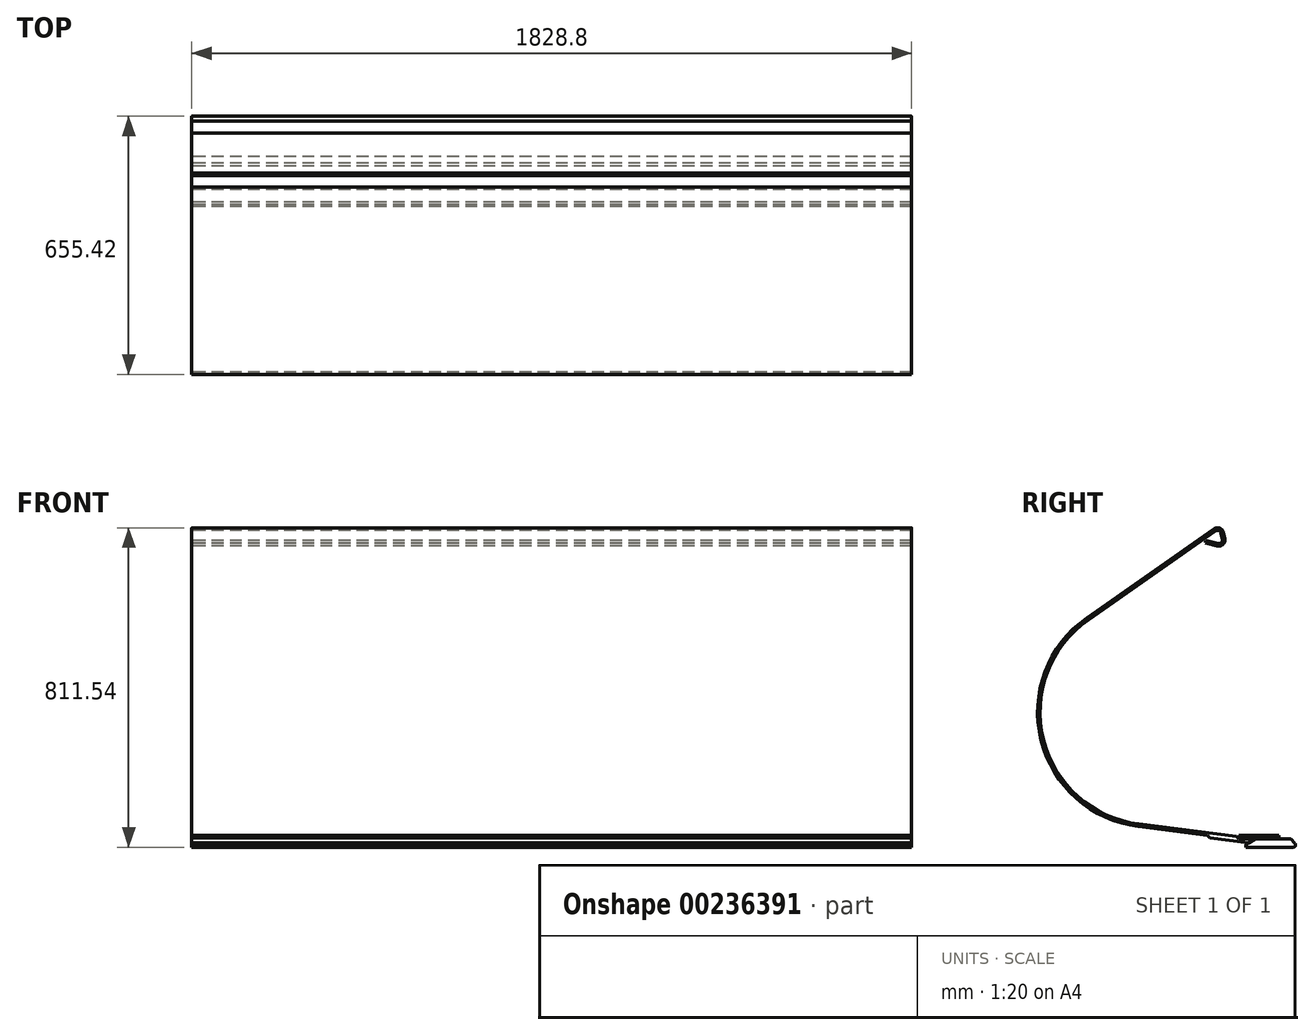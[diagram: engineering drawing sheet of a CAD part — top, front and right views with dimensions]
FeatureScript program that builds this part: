
annotation { "Feature Type Name" : "Feature", "Feature Type Description" : "" }
export const myFeature = defineFeature(function(context is Context, id is Id, definition is map)
    precondition{}
    {
        {
            var Q0;
            Q0=qCreatedBy(makeId("Right.planeOp"),FACE);
            var sketch = newSketch(context, id + "F0", { "sketchPlane" : qUnion([Q0])});
            skLineSegment(sketch, "E0", {"start": v(-127, 0) * mm, "end": v(-6, 0) * mm});
            skArc(sketch, "E1", {"start": v(-6, 0) * mm, "mid": v(-0.46, 3.7) * mm, "end": v(-1.76, 10.24) * mm});
            skLineSegment(sketch, "E2", {"start": v(-1.76, 10.24) * mm, "end": v(-12.51, 21) * mm});
            skLineSegment(sketch, "E3", {"start": v(-12.51, 21) * mm, "end": v(-102, 21) * mm});
            skLineSegment(sketch, "E4", {"start": v(-102, 21) * mm, "end": v(-127, 6.57) * mm});
            skLineSegment(sketch, "E5", {"start": v(-127, 6.57) * mm, "end": v(-127, 0) * mm});
            skSolve(sketch);
        }
        {
            var Q0;
            Q0 = qSketchRegion(id + "F0", true);
            extrude(context, id + "F1", {"entities" : qUnion([Q0]), "endBound" : BoundingType.SYMMETRIC, "depth" : 1828.8 * mm});
        }
        {
            var Q0;
            Q0=qCreatedBy(makeId("Right.planeOp"),FACE);
            var sketch = newSketch(context, id + "F2", { "sketchPlane" : qUnion([Q0])});
            skLineSegment(sketch, "E6.bottom", {"start": v(-42, 21) * mm, "end": v(-143.6, 21) * mm});
            skLineSegment(sketch, "E6.top", {"start": v(-42, 30.52) * mm, "end": v(-143.6, 30.52) * mm});
            skLineSegment(sketch, "E6.left", {"start": v(-42, 21) * mm, "end": v(-42, 30.52) * mm});
            skLineSegment(sketch, "E6.right", {"start": v(-143.6, 21) * mm, "end": v(-143.6, 30.52) * mm});
            skSolve(sketch);
        }
        {
            var Q0;
            Q0 = qSketchRegion(id + "F2", true);
            extrude(context, id + "F3", {"entities" : qUnion([Q0]), "endBound" : BoundingType.SYMMETRIC, "depth" : 1828.8 * mm});
        }
        {
            var Q0;
            Q0=qCreatedBy(makeId("Right.planeOp"),FACE);
            var sketch = newSketch(context, id + "F4", { "sketchPlane" : qUnion([Q0])});
            skLineSegment(sketch, "E7", {"start": v(-102, 21) * mm, "end": v(-143.6, 21) * mm});
            skLineSegment(sketch, "E8", {"start": v(-143.6, 21) * mm, "end": v(-149.95, 27.35) * mm});
            skArc(sketch, "E9", {"start": v(-399.27, 52.39) * mm, "mid": v(-646.84, 272.5) * mm, "end": v(-530.58, 582.69) * mm});
            skLineSegment(sketch, "E10", {"start": v(-530.58, 582.69) * mm, "end": v(-207.88, 808.64) * mm});
            skLineSegment(sketch, "E11", {"start": v(-183.11, 799.14) * mm, "end": v(-179.74, 784.52) * mm});
            skLineSegment(sketch, "E12", {"start": v(-199.47, 765.47) * mm, "end": v(-229.43, 773.5) * mm});
            skLineSegment(sketch, "E13", {"start": v(-186.7, 814.73) * mm, "end": v(0, 6) * mm, "construction": true});
            skPoint(sketch, "E14.visualSharp", {"position": v(-186.7, 814.73) * mm});
            skArc(sketch, "E14.filletArc", {"start": v(-183.11, 799.14) * mm, "mid": v(-192.97, 810.48) * mm, "end": v(-207.88, 808.64) * mm});
            skPoint(sketch, "E15.visualSharp", {"position": v(-173.75, 758.58) * mm});
            skArc(sketch, "E15.filletArc", {"start": v(-199.47, 765.47) * mm, "mid": v(-184.21, 769.41) * mm, "end": v(-179.74, 784.52) * mm});
            skLineSegment(sketch, "E16", {"start": v(-186.7, 814.73) * mm, "end": v(-530.58, 735.34) * mm, "construction": true});
            skLineSegment(sketch, "E17", {"start": v(-102, 21) * mm, "end": v(-118.5, 11.47) * mm});
            skLineSegment(sketch, "E18", {"start": v(-118.5, 11.47) * mm, "end": v(-217.71, 23.99) * mm});
            skLineSegment(sketch, "E19", {"start": v(-217.71, 23.99) * mm, "end": v(-224.02, 30.29) * mm});
            skLineSegment(sketch, "E20", {"start": v(-399.27, 52.39) * mm, "end": v(-224.02, 30.29) * mm});
            skLineSegment(sketch, "E21.0", {"start": v(-398.48, 58.69) * mm, "end": v(-149.95, 27.35) * mm});
            skArc(sketch, "E21.1", {"start": v(-398.48, 58.69) * mm, "mid": v(-640.68, 274.02) * mm, "end": v(-526.93, 577.49) * mm});
            skLineSegment(sketch, "E21.2", {"start": v(-526.93, 577.49) * mm, "end": v(-204.24, 803.44) * mm});
            skLineSegment(sketch, "E21.3", {"start": v(-197.82, 771.6) * mm, "end": v(-227.78, 779.63) * mm});
            skArc(sketch, "E21.4", {"start": v(-197.82, 771.6) * mm, "mid": v(-188.62, 773.98) * mm, "end": v(-185.92, 783.1) * mm});
            skLineSegment(sketch, "E21.5", {"start": v(-189.3, 797.7) * mm, "end": v(-185.92, 783.1) * mm});
            skArc(sketch, "E21.6", {"start": v(-189.3, 797.7) * mm, "mid": v(-195.24, 804.55) * mm, "end": v(-204.24, 803.44) * mm});
            skLineSegment(sketch, "E22", {"start": v(-227.78, 779.63) * mm, "end": v(-229.43, 773.5) * mm});
            skLineSegment(sketch, "E23", {"start": v(-176.14, 768.93) * mm, "end": v(-291.59, 742.28) * mm, "construction": true});
            skLineSegment(sketch, "E24", {"start": v(-179.74, 784.52) * mm, "end": v(-102, 21) * mm, "construction": true});
            skSolve(sketch);
        }
        {
            var Q0;
            Q0=makeQuery(id+"F4.imprint","IMPRINT",FACE,{"disambiguationData":[TD([[makeQuery(id+"F4.imprint","IMPRINT",EDGE,{"derivedFrom":sQuery(id+"F4.wireOp",EDGE,"E7")}),1.0]])]});
            extrude(context, id + "F5", {"entities" : qUnion([Q0]), "endBound" : BoundingType.SYMMETRIC, "depth" : 1828.8 * mm});
        }
    });
